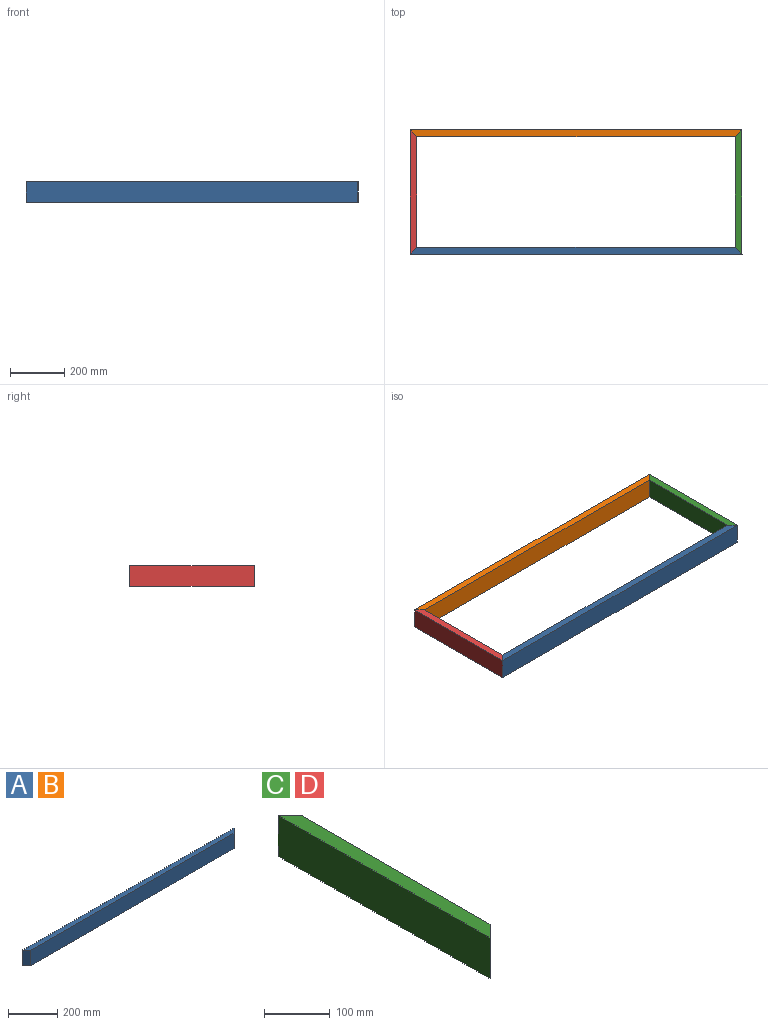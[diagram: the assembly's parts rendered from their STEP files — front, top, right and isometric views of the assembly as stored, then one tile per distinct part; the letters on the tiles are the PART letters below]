
ASSEMBLY  parts=4 mates=4
PART A: 6 faces, bbox 1219.2x25.4x76.2 mm
  f0: plane 1168.4x76.2mm, normal (0,-1,0), area 89032.1mm2, adj f2,f3,f4,f5
  f1: plane 1219.2x76.2mm, normal (0,1,0), area 92903mm2, adj f2,f3,f4,f5
  f2: plane 1219.2x25.4mm, normal (0,0,1), area 30322.5mm2, adj f0,f1,f4,f5
  f3: plane 1219.2x25.4mm, normal (0,0,-1), area 30322.5mm2, adj f0,f1,f4,f5
  f4: plane 76.2x25.4mm, normal (0.71,-0.71,0), area 2737.2mm2, adj f0,f1,f2,f3
  f5: plane 76.2x25.4mm, normal (-0.71,-0.71,0), area 2737.2mm2, adj f0,f1,f2,f3
PART B: same geometry as A
PART C: 6 faces, bbox 25.4x457.2x76.2 mm
  f0: plane 457.2x76.2mm, normal (-1,0,0), area 34838.6mm2, adj f2,f3,f4,f5
  f1: plane 406.4x76.2mm, normal (1,0,0), area 30967.7mm2, adj f2,f3,f4,f5
  f2: plane 457.2x25.4mm, normal (0,0,1), area 10967.7mm2, adj f0,f1,f4,f5
  f3: plane 457.2x25.4mm, normal (0,0,-1), area 10967.7mm2, adj f0,f1,f4,f5
  f4: plane 76.2x25.4mm, normal (0.71,0.71,0), area 2737.2mm2, adj f0,f1,f2,f3
  f5: plane 76.2x25.4mm, normal (0.71,-0.71,0), area 2737.2mm2, adj f0,f1,f2,f3
PART D: same geometry as C
PLACE A rot(axis=(0,0,1),180deg) t=(819.95,454.88,-234.98)mm
PLACE B t=(-629.07,135.73,-234.98)mm
PLACE C rot(axis=(0,-1,0),180deg) t=(595.91,71.76,-158.78)mm
PLACE D t=(-405.03,71.76,-234.98)mm
MATE parallel C.f1 <-> D.f0  axis (-1,0,0) through (679.64,295.3,-196.88)mm
MATE fastened C.f5 <-> A.f5  axis (-0.71,-0.71,0) through (692.34,79.4,-196.88)mm
MATE fastened D.f5 <-> A.f4  axis (0.71,-0.71,0) through (-501.46,79.4,-196.88)mm
MATE fastened B.f5 <-> D.f4  axis (-0.71,-0.71,0) through (-501.46,511.2,-196.88)mm
